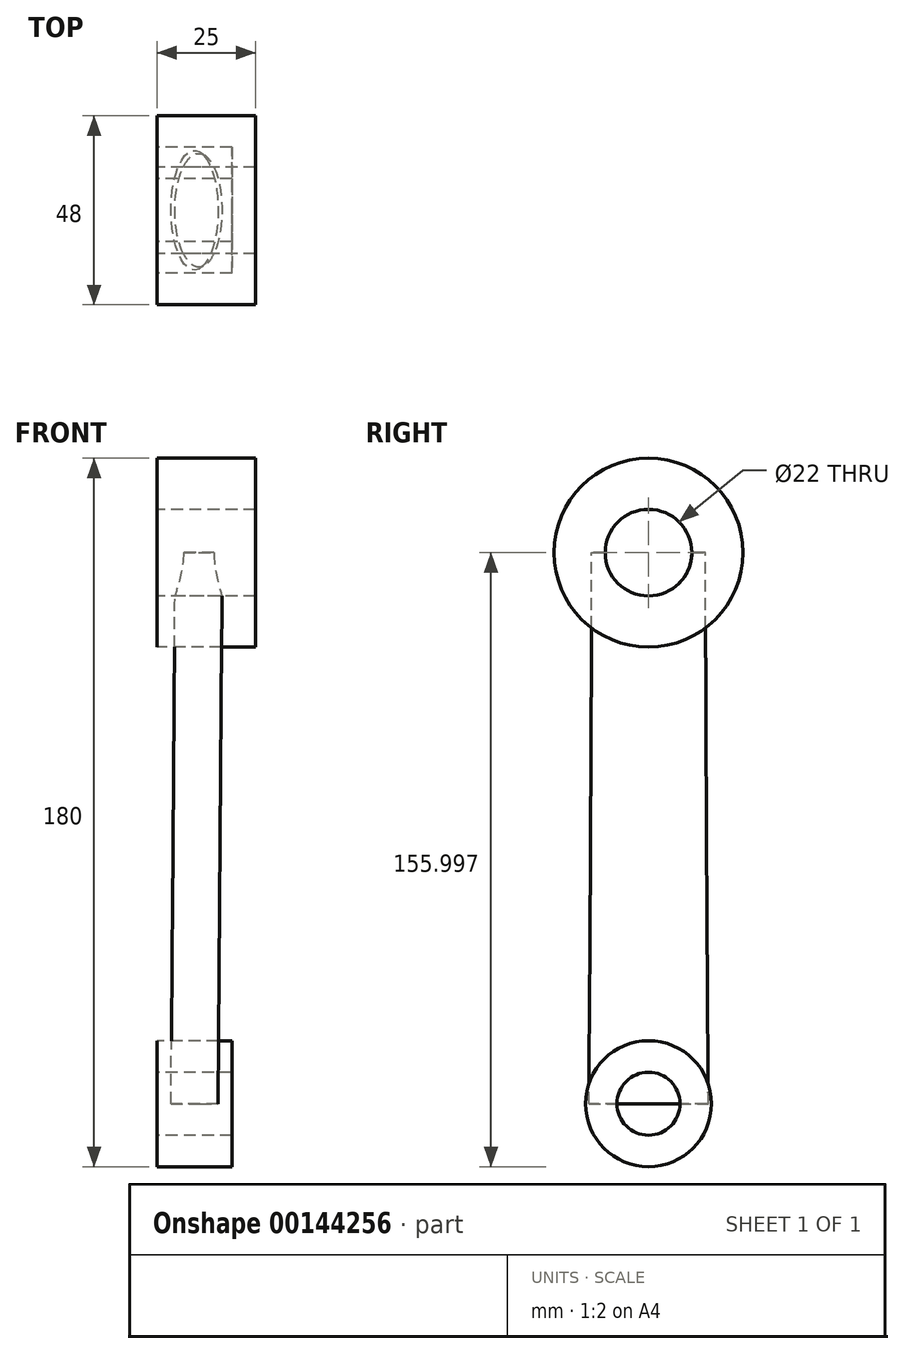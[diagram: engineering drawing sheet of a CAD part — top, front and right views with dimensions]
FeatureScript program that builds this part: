
annotation { "Feature Type Name" : "Feature", "Feature Type Description" : "" }
export const myFeature = defineFeature(function(context is Context, id is Id, definition is map)
    precondition{}
    {
        {
            var Q0;
            Q0=qCreatedBy(makeId("Right.planeOp"),FACE);
            var sketch = newSketch(context, id + "F0", { "sketchPlane" : qUnion([Q0])});
            skCircle(sketch, "E0", {"center": v(0, 88.89) * mm, "radius": 24 * mm});
            skCircle(sketch, "E1", {"center": v(0, 88.89) * mm, "radius": 11 * mm});
            skCircle(sketch, "E2", {"center": v(0, -51.11) * mm, "radius": 16 * mm});
            skCircle(sketch, "E3", {"center": v(0, -51.11) * mm, "radius": 8 * mm});
            skLineSegment(sketch, "E4", {"start": v(0, 88.89) * mm, "end": v(0, -51.11) * mm, "construction": true});
            skSolve(sketch);
        }
        {
            var Q0;
            Q0=makeQuery(id+"F0.imprint","IMPRINT",FACE,{"disambiguationData":[TD([[makeQuery(id+"F0.imprint","IMPRINT",EDGE,{"derivedFrom":sQuery(id+"F0.wireOp",EDGE,"E0")}),1.0]])]});
            extrude(context, id + "F1", {"entities" : qUnion([Q0]), "depth" : 25 * mm});
        }
        {
            var Q0;
            Q0=makeQuery(id+"F0.imprint","IMPRINT",FACE,{"disambiguationData":[TD([[makeQuery(id+"F0.imprint","IMPRINT",EDGE,{"derivedFrom":sQuery(id+"F0.wireOp",EDGE,"E2")}),1.0]])]});
            extrude(context, id + "F2", {"entities" : qUnion([Q0]), "depth" : 19 * mm});
        }
        {
            var Q0;
            Q0=qCreatedBy(makeId("Right.planeOp"),FACE);
            var sketch = newSketch(context, id + "F3", { "sketchPlane" : qUnion([Q0])});
            skLineSegment(sketch, "E5", {"start": v(26.29, 88.89) * mm, "end": v(-31.09, 88.89) * mm, "construction": true});
            skLineSegment(sketch, "E6", {"start": v(20.58, -51.11) * mm, "end": v(-24.57, -51.11) * mm, "construction": true});
            skSolve(sketch);
        }
        {
            var Q0;
            Q0=sQuery(id+"F3.wireOp",EDGE,"E5");
            cPlane(context, id + "F4", {"entities" : qUnion([Q0]), "cplaneType" : CPlaneType.LINE_ANGLE, "offset" : 25 * mm, "angle" : 0 * degree, "width" : 150 * mm, "height" : 150 * mm});
        }
        {
            var Q0;
            Q0=qCreatedBy(id+"F4.planeOp",FACE);
            var sketch = newSketch(context, id + "F5", { "sketchPlane" : qUnion([Q0])});
            skEllipse(sketch, "E7", {"center": v(10.58, 0) * mm, "majorRadius": 14.43 * mm, "minorRadius": 6 * mm, "majorAxis": v(0, -1)});
            skSolve(sketch);
        }
        {
            var Q0;
            Q0=sQuery(id+"F3.wireOp",EDGE,"E6");
            cPlane(context, id + "F6", {"entities" : qUnion([Q0]), "cplaneType" : CPlaneType.LINE_ANGLE, "offset" : 25 * mm, "angle" : 0 * degree, "width" : 150 * mm, "height" : 150 * mm});
        }
        {
            var Q0;
            Q0=qCreatedBy(id+"F6.planeOp",FACE);
            var sketch = newSketch(context, id + "F7", { "sketchPlane" : qUnion([Q0])});
            skEllipse(sketch, "E8", {"center": v(9.5, 0) * mm, "majorRadius": 15.18 * mm, "minorRadius": 6 * mm, "majorAxis": v(0, 1)});
            skSolve(sketch);
        }
        {
            var Q0;
            Q0=makeQuery(id+"F5.imprint","IMPRINT",FACE,{"disambiguationData":[TD([[makeQuery(id+"F5.imprint","IMPRINT",EDGE,{"derivedFrom":sQuery(id+"F5.wireOp",EDGE,"E7")}),1.0]])]});
            var Q1;
            Q1=makeQuery(id+"F7.imprint","IMPRINT",FACE,{"disambiguationData":[TD([[makeQuery(id+"F7.imprint","IMPRINT",EDGE,{"derivedFrom":sQuery(id+"F7.wireOp",EDGE,"E8")}),1.0]])]});
            loft(context, id + "F8", {"sheetProfilesArray" : [{ "sheetProfileEntities" : qUnion([Q0]) }, { "sheetProfileEntities" : qUnion([Q1]) }]});
        }
        {
            var Q0;
            Q0=makeQuery(id+"F0.imprint","IMPRINT",FACE,{"disambiguationData":[TD([[makeQuery(id+"F0.imprint","IMPRINT",EDGE,{"derivedFrom":sQuery(id+"F0.wireOp",EDGE,"E1")}),1.0]])]});
            var sketch = newSketch(context, id + "F9", { "sketchPlane" : qUnion([Q0])});
            skCircle(sketch, "E9", {"center": v(0, 88.89) * mm, "radius": 11 * mm});
            skSolve(sketch);
        }
        {
            var Q0;
            Q0 = qSketchRegion(id + "F9", true);
            extrude(context, id + "F10", {"entities" : qUnion([Q0]), "operationType" : NewBodyOperationType.REMOVE, "endBound" : BoundingType.THROUGH_ALL, "depth" : 25 * mm});
        }
    });
